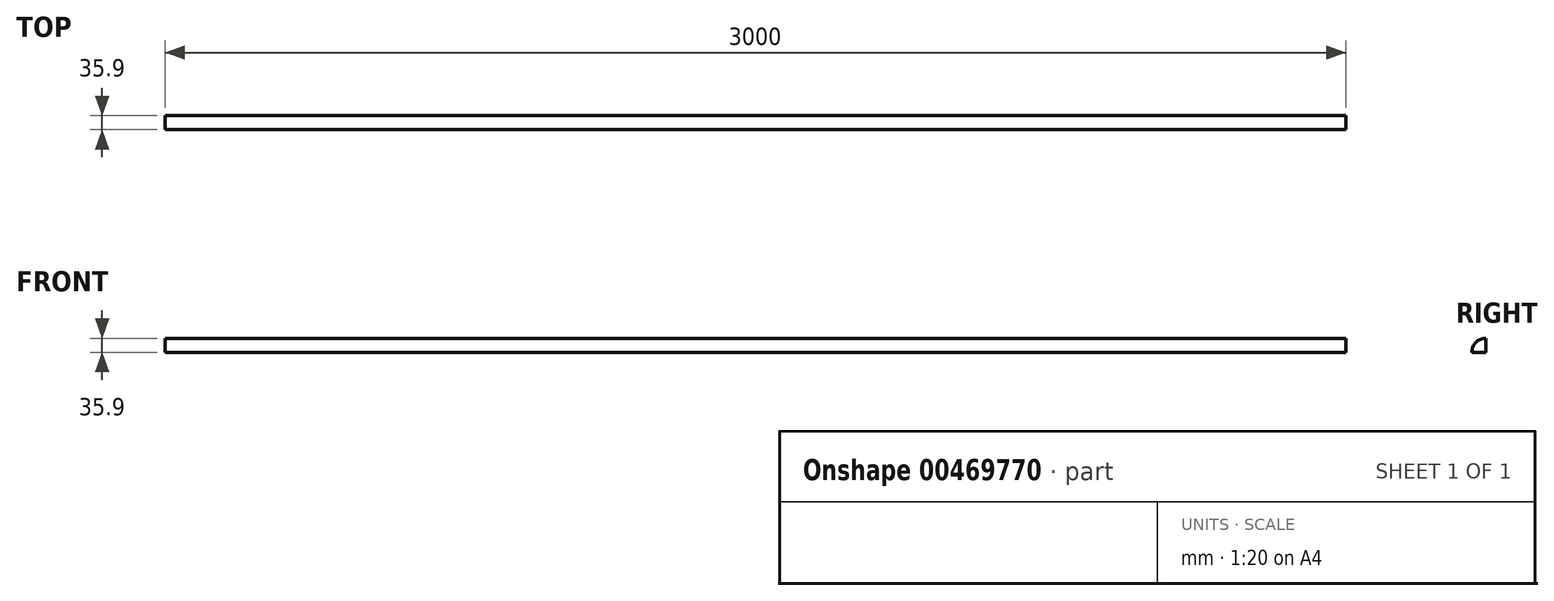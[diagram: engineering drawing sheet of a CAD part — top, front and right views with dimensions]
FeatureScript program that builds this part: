
annotation { "Feature Type Name" : "Feature", "Feature Type Description" : "" }
export const myFeature = defineFeature(function(context is Context, id is Id, definition is map)
    precondition{}
    {
        {
            var Q0;
            Q0=qCreatedBy(makeId("Front.planeOp"),FACE);
            var sketch = newSketch(context, id + "F0", { "sketchPlane" : qUnion([Q0])});
            skLineSegment(sketch, "E0.bottom", {"start": v(0, 35.9) * mm, "end": v(3000, 35.9) * mm});
            skLineSegment(sketch, "E0.top", {"start": v(0, 0) * mm, "end": v(3000, 0) * mm});
            skLineSegment(sketch, "E0.left", {"start": v(0, 35.9) * mm, "end": v(0, 0) * mm});
            skLineSegment(sketch, "E0.right", {"start": v(3000, 35.9) * mm, "end": v(3000, 0) * mm});
            skLineSegment(sketch, "E1.bottom", {"start": v(0, 24.08) * mm, "end": v(0, 24.08) * mm});
            skLineSegment(sketch, "E1.top", {"start": v(0, 35.9) * mm, "end": v(0, 35.9) * mm});
            skLineSegment(sketch, "E1.left", {"start": v(0, 35.9) * mm, "end": v(0, 24.08) * mm});
            skLineSegment(sketch, "E1.right", {"start": v(0, 35.9) * mm, "end": v(0, 24.08) * mm});
            skSolve(sketch);
        }
        {
            var Q0;
            Q0=makeQuery(id+"F0.imprint","IMPRINT",FACE,{"disambiguationData":[TD([[makeQuery(id+"F0.imprint","IMPRINT",EDGE,{"derivedFrom":sQuery(id+"F0.wireOp",EDGE,"E0.bottom")}),-1.0]])]});
            var Q1;
            Q1=sQuery(id+"F0.wireOp",EDGE,"E0.bottom");
            var Q2;
            Q2=sQuery(id+"F0.wireOp",EDGE,"E0.top");
            var Q3;
            Q3=sQuery(id+"F0.wireOp",EDGE,"E0.top");
            revolve(context, id + "F1", {"entities" : qUnion([Q0]), "surfaceEntities" : qUnion([Q1, Q2]), "axis" : qUnion([Q3]), "revolveType" : RevolveType.ONE_DIRECTION, "angle" : 90 * degree});
        }
    });
